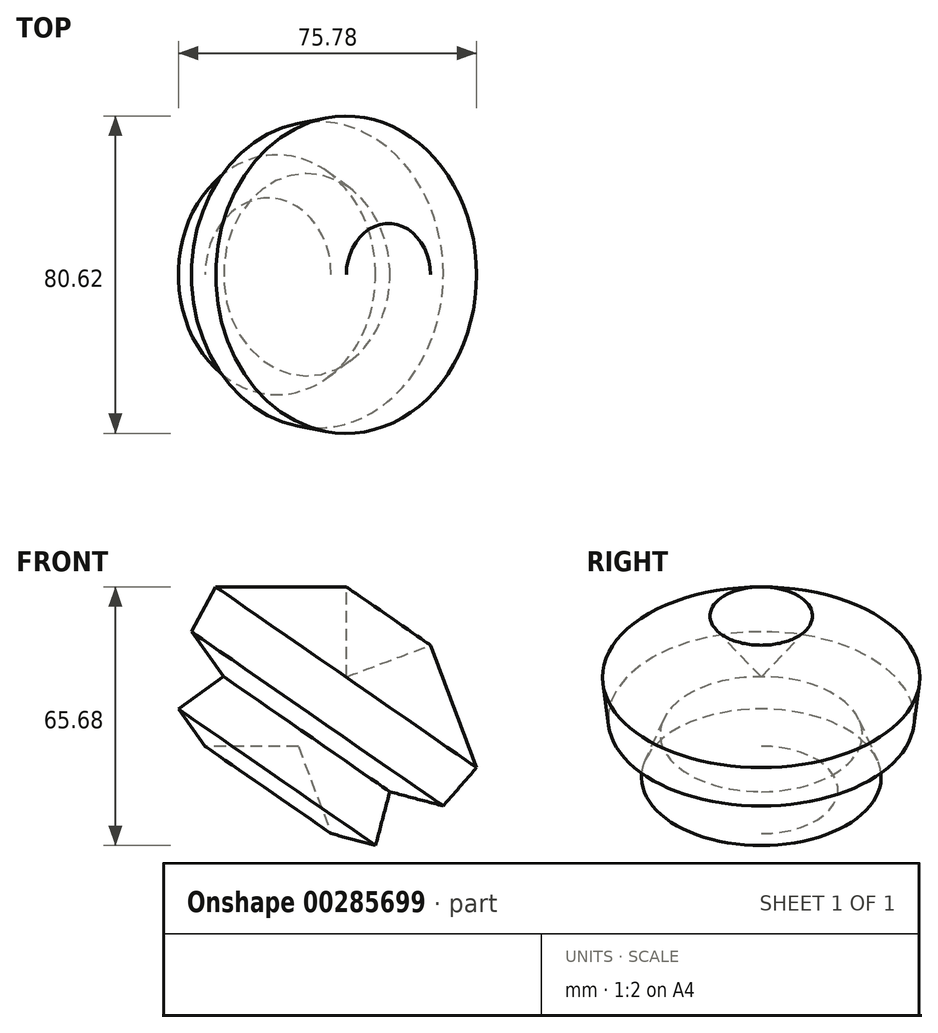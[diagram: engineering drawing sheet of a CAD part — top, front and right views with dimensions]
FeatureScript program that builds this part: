
annotation { "Feature Type Name" : "Feature", "Feature Type Description" : "" }
export const myFeature = defineFeature(function(context is Context, id is Id, definition is map)
    precondition{}
    {
        {
            var Q0;
            Q0=qCreatedBy(makeId("Front.planeOp"),FACE);
            var sketch = newSketch(context, id + "F0", { "sketchPlane" : qUnion([Q0])});
            skLineSegment(sketch, "E0", {"start": v(0, 17.62) * mm, "end": v(-12.2, 0) * mm});
            skLineSegment(sketch, "E1", {"start": v(-12.2, 0) * mm, "end": v(-35.91, 0) * mm});
            skLineSegment(sketch, "E2", {"start": v(-35.91, 0) * mm, "end": v(-42.69, 9.49) * mm});
            skLineSegment(sketch, "E3", {"start": v(-42.69, 9.49) * mm, "end": v(-31.2, 17.7) * mm});
            skLineSegment(sketch, "E4", {"start": v(-31.2, 17.7) * mm, "end": v(-39.36, 29.12) * mm});
            skLineSegment(sketch, "E5", {"start": v(-39.36, 29.12) * mm, "end": v(-33.2, 40.48) * mm});
            skLineSegment(sketch, "E6", {"start": v(-33.2, 40.48) * mm, "end": v(0, 40.48) * mm});
            skLineSegment(sketch, "E7", {"start": v(0, 40.48) * mm, "end": v(0, 17.62) * mm});
            skSolve(sketch);
        }
        {
            var Q0;
            Q0 = qSketchRegion(id + "F0", true);
            var Q1;
            Q1=sQuery(id+"F0.wireOp",EDGE,"E0");
            revolve(context, id + "F1", {"entities" : qUnion([Q0]), "axis" : qUnion([Q1]), "revolveType" : RevolveType.FULL});
        }
    });
